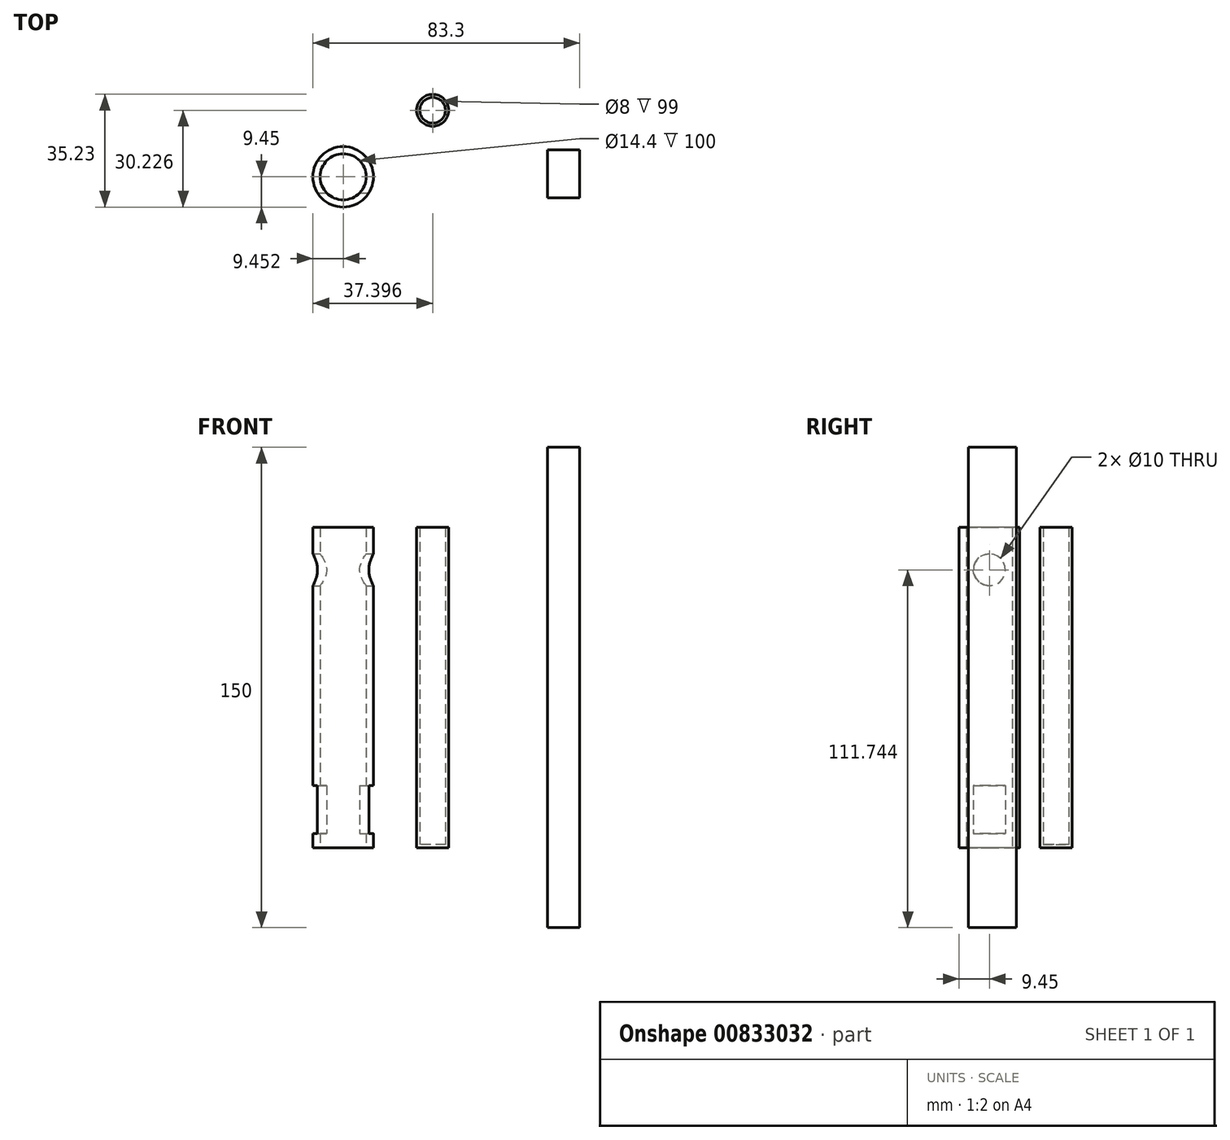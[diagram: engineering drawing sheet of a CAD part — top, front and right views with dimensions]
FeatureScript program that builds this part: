
annotation { "Feature Type Name" : "Feature", "Feature Type Description" : "" }
export const myFeature = defineFeature(function(context is Context, id is Id, definition is map)
    precondition{}
    {
        {
            var Q0;
            Q0=qCreatedBy(makeId("Top.planeOp"),FACE);
            var sketch = newSketch(context, id + "F0", { "sketchPlane" : qUnion([Q0])});
            skCircle(sketch, "E0", {"center": v(-46, 0) * mm, "radius": 7.2 * mm});
            skCircle(sketch, "E1", {"center": v(-46, 0) * mm, "radius": 9.45 * mm});
            skSolve(sketch);
        }
        {
            var Q0;
            Q0=makeQuery(id+"F0.imprint","IMPRINT",FACE,{"disambiguationData":[TD([[makeQuery(id+"F0.imprint","IMPRINT",EDGE,{"derivedFrom":sQuery(id+"F0.wireOp",EDGE,"E0")}),-1.0]])]});
            extrude(context, id + "F1", {"entities" : qUnion([Q0]), "endBound" : BoundingType.SYMMETRIC, "depth" : 100 * mm, "offsetDistance" : 25 * mm});
        }
        {
            var Q0;
            Q0=qCreatedBy(makeId("Right.planeOp"),FACE);
            var sketch = newSketch(context, id + "F2", { "sketchPlane" : qUnion([Q0])});
            skCircle(sketch, "E2", {"center": v(0, 36.74) * mm, "radius": 5 * mm});
            skLineSegment(sketch, "E3.bottom", {"start": v(-5, -30.57) * mm, "end": v(5, -30.57) * mm});
            skLineSegment(sketch, "E3.top", {"start": v(-5, -45.57) * mm, "end": v(5, -45.57) * mm});
            skLineSegment(sketch, "E3.left", {"start": v(-5, -30.57) * mm, "end": v(-5, -45.57) * mm});
            skLineSegment(sketch, "E3.right", {"start": v(5, -30.57) * mm, "end": v(5, -45.57) * mm});
            skSolve(sketch);
        }
        {
            var Q0;
            Q0=makeQuery(id+"F2.imprint","IMPRINT",FACE,{"disambiguationData":[TD([[makeQuery(id+"F2.imprint","IMPRINT",EDGE,{"derivedFrom":sQuery(id+"F2.wireOp",EDGE,"E2")}),1.0]])]});
            var Q1;
            Q1=makeQuery(id+"F2.imprint","IMPRINT",FACE,{"disambiguationData":[TD([[makeQuery(id+"F2.imprint","IMPRINT",EDGE,{"derivedFrom":sQuery(id+"F2.wireOp",EDGE,"E3.bottom")}),-1.0]])]});
            extrude(context, id + "F3", {"entities" : qUnion([Q0, Q1]), "operationType" : NewBodyOperationType.REMOVE, "endBound" : BoundingType.SYMMETRIC, "oppositeDirection" : true, "depth" : 500 * mm, "offsetDistance" : 25 * mm});
        }
        {
            var Q0;
            Q0=qCreatedBy(makeId("Top.planeOp"),FACE);
            var sketch = newSketch(context, id + "F4", { "sketchPlane" : qUnion([Q0])});
            skCircle(sketch, "E4", {"center": v(-18.05, 20.78) * mm, "radius": 5 * mm});
            skSolve(sketch);
        }
        {
            var Q0;
            Q0=makeQuery(id+"F4.imprint","IMPRINT",FACE,{"disambiguationData":[TD([[makeQuery(id+"F4.imprint","IMPRINT",EDGE,{"derivedFrom":sQuery(id+"F4.wireOp",EDGE,"E4")}),1.0]])]});
            extrude(context, id + "F5", {"entities" : qUnion([Q0]), "endBound" : BoundingType.SYMMETRIC, "depth" : 100 * mm, "offsetDistance" : 25 * mm});
        }
        {
            var Q0;
            Q0=makeQuery(id+"F5.opExtrude","CAP_FACE",FACE,{"disambiguationData":[OSD([sQuery(id+"F4.wireOp",EDGE,"E4")])],"isStart":false});
            shell(context, id + "F6", {"entities" : qUnion([Q0]), "thickness" : 1 * mm});
        }
        {
            var Q0;
            Q0=qCreatedBy(makeId("Top.planeOp"),FACE);
            var sketch = newSketch(context, id + "F7", { "sketchPlane" : qUnion([Q0])});
            skLineSegment(sketch, "E5.bottom", {"start": v(17.85, 8.38) * mm, "end": v(27.85, 8.38) * mm});
            skLineSegment(sketch, "E5.top", {"start": v(17.85, -6.62) * mm, "end": v(27.85, -6.62) * mm});
            skLineSegment(sketch, "E5.left", {"start": v(17.85, 8.38) * mm, "end": v(17.85, -6.62) * mm});
            skLineSegment(sketch, "E5.right", {"start": v(27.85, 8.38) * mm, "end": v(27.85, -6.62) * mm});
            skSolve(sketch);
        }
        {
            var Q0;
            Q0 = qSketchRegion(id + "F7", true);
            extrude(context, id + "F8", {"entities" : qUnion([Q0]), "endBound" : BoundingType.SYMMETRIC, "depth" : 150 * mm, "offsetDistance" : 25 * mm});
        }
    });
